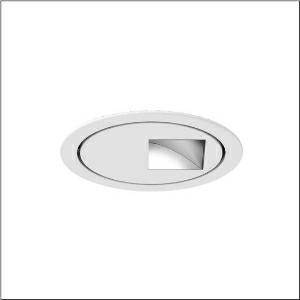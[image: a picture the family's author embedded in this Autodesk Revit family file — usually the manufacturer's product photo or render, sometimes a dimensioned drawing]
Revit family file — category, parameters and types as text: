
# Revit family: lunis_11_mini_round_51dk11cd2wg21
name_source: partatom
category: Lighting Fixtures
units: mm (PartAtom-declared; Revit-internal decimal feet)

## family parameters
Cut with Voids When Loaded = No
Host = Face
Light Source = No
Part Type = Normal
Room Calculation Point = No
Round Connector Dimension = Use Diameter
Shared = No

## types (1)
- Lunis 11 mini round (1 x LED 4000K / CRI = 80 (unbekannt), 2470 lm, 4000K)
    Apparent Load = 28 VA
    CIE Flux Codes = 44 77 97 100 100
    Color Rendering = 80
    Color Temperature = 4000K
    Default Elevation = 1800 mm
    Description = Lunis 11 mini round, downlight, light control with wallwasher, of highly reflective aluminium, highly specular, light emission: direct distribution, LED rated luminous flux: 2.470lm, light colour: 840, control gear: ECG, with terminal, 5-pole, mains connection: 220..230V, AC/DC, 0/50..60Hz, LED module, luminaire module, of aluminium, highly specular, white, diameter: 176mm, clamping range: 1..40mm, recessing ring, of plastic, traffic white (RAL 9016), protection rating (complete): IP20, insulation class (complete): insulation class II (safety insulation), certification: CE, permissible ambient temperature for indoor applications: 0..+35°C, packaging unit: 1 piece
    Height = 0 mm  [stored 0 ft]
    Lamp = 1 x LED 4000K / CRI >= 80 (unbekannt)
    Lamp Light Flux = 2470 lm
    Lamp count = 1
    Length = 176 mm
    Luminous efficacy = 89 lm/W
    Manufacturer = Siteco
    ModVariant = No
    Model = 51DK11CD2WG21
    Mounting Place = Ceiling
    Mounting Type = Recessed
    Number of Poles = 1
    OnlyDefault = Yes
    Power Factor = 1
    Product Name = Lunis 11 mini round
    Product group = downlight | ceiling recessed
    ProductGroupID = 402
    Protection Class = Protection class II
    Protection Degree = IP 20
    RLX_Detail_Level = 1
    RlxData = <blob elided: 59309 chars, md5=63843cd5>
    Socket = socket
    Standby Power = 0 W
    System Light Flux = 2470 lm
    System Power = 28 W
    Type Comments = Product without accessories
    Type Image = l_1004772.jpg
    URL = http://relux.com
    VarID = ---
    Voltage = 0 V
    Weight = 0.00 kg
    Width = 176 mm

note: [stored X ft] marks values corroborated as IEEE doubles in the binary element streams (Revit-internal decimal feet)

## geometry (parser evidence)
native form markers: Blend x4, Sweep x12
no freeform markers — native parametric forms only
